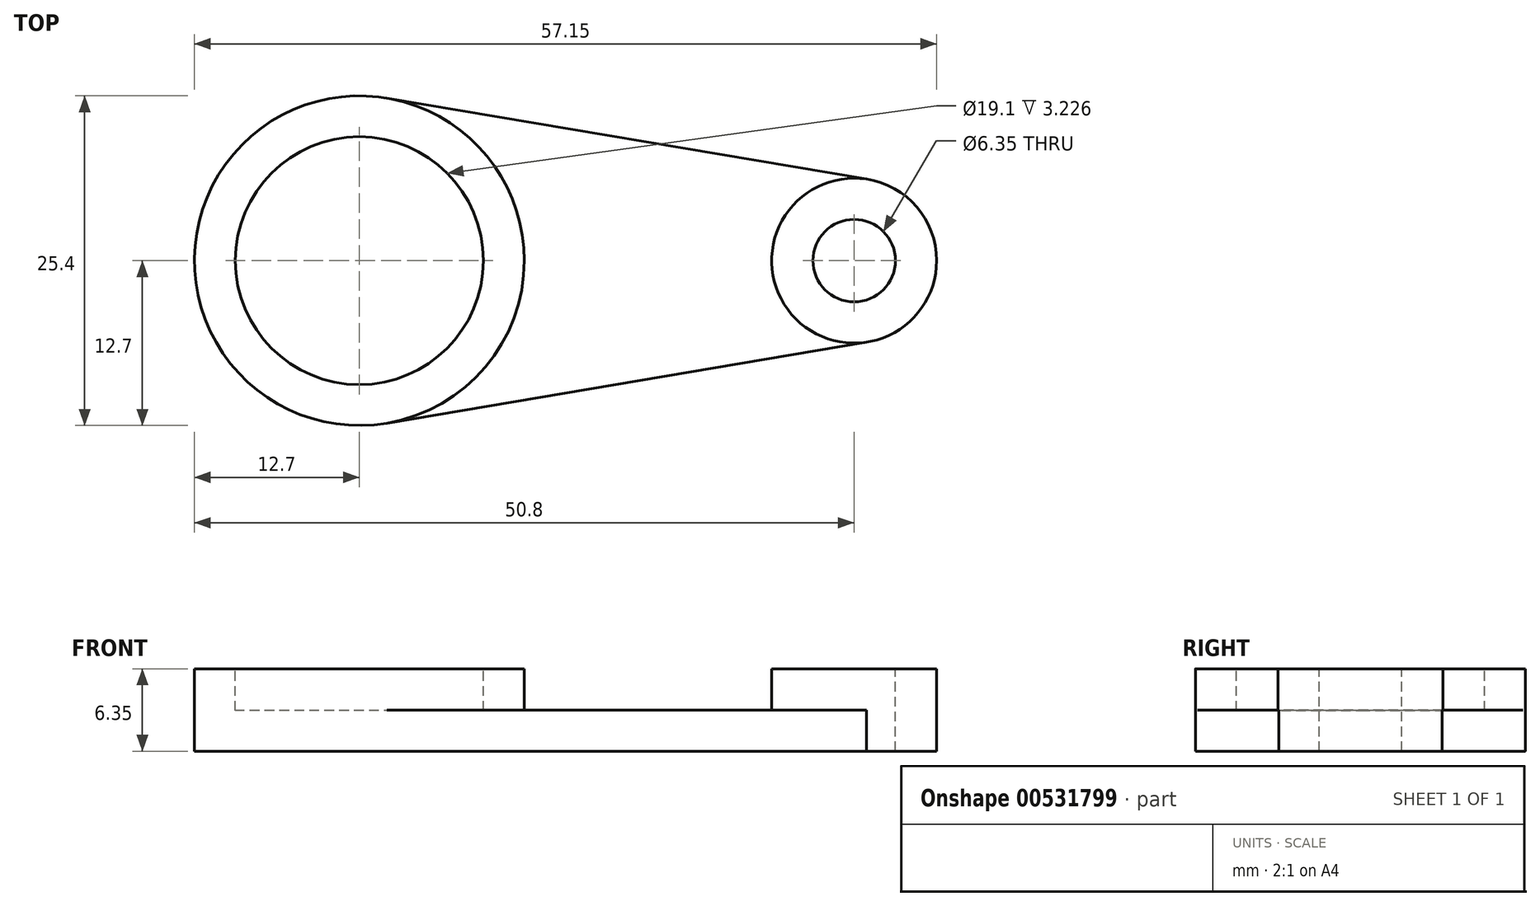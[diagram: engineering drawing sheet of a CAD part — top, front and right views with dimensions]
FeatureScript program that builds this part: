
annotation { "Feature Type Name" : "Feature", "Feature Type Description" : "" }
export const myFeature = defineFeature(function(context is Context, id is Id, definition is map)
    precondition{}
    {
        {
            var Q0;
            Q0=qCreatedBy(makeId("Top.planeOp"),FACE);
            var sketch = newSketch(context, id + "F0", { "sketchPlane" : qUnion([Q0])});
            skCircle(sketch, "E0", {"center": v(0, 0) * mm, "radius": 12.7 * mm});
            skCircle(sketch, "E1", {"center": v(38.1, 0) * mm, "radius": 6.35 * mm});
            skLineSegment(sketch, "E2", {"start": v(39.05, -6.28) * mm, "end": v(2.12, -12.52) * mm});
            skLineSegment(sketch, "E3", {"start": v(2.12, 12.52) * mm, "end": v(39.05, 6.28) * mm});
            skSolve(sketch);
        }
        {
            var Q0;
            Q0 = qSketchRegion(id + "F0", true);
            extrude(context, id + "F1", {"entities" : qUnion([Q0]), "depth" : 3.17 * mm, "offsetDistance" : 25.4 * mm});
        }
        {
            var Q0;
            Q0=makeQuery(id+"F1.opExtrude","CAP_FACE",FACE,{"disambiguationData":[OSD([sQuery(id+"F0.wireOp",EDGE,"E0"),sQuery(id+"F0.wireOp",EDGE,"E1"),sQuery(id+"F0.wireOp",EDGE,"E2"),sQuery(id+"F0.wireOp",EDGE,"E3")])],"isStart":false});
            var sketch = newSketch(context, id + "F2", { "sketchPlane" : qUnion([Q0])});
            skArc(sketch, "E4.0", {"start": v(39.05, -6.28) * mm, "mid": v(44.45, 0) * mm, "end": v(39.05, 6.28) * mm});
            skCircle(sketch, "E5", {"center": v(38.1, 0) * mm, "radius": 6.35 * mm});
            skArc(sketch, "E6.0", {"start": v(2.12, 12.52) * mm, "mid": v(-12.7, 0) * mm, "end": v(2.12, -12.52) * mm});
            skCircle(sketch, "E7", {"center": v(0, 0) * mm, "radius": 12.7 * mm});
            skSolve(sketch);
        }
        {
            var Q0;
            Q0 = qSketchRegion(id + "F2", true);
            extrude(context, id + "F3", {"entities" : qUnion([Q0]), "operationType" : NewBodyOperationType.ADD, "depth" : 3.17 * mm, "offsetDistance" : 25.4 * mm});
        }
        {
            var Q0;
            Q0=makeQuery(id+"F3.opExtrude","CAP_FACE",FACE,{"disambiguationData":[OSD([sQuery(id+"F2.wireOp",EDGE,"E7")])],"isStart":false});
            var sketch = newSketch(context, id + "F4", { "sketchPlane" : qUnion([Q0])});
            skCircle(sketch, "E8", {"center": v(0, 0) * mm, "radius": 9.55 * mm});
            skSolve(sketch);
        }
        {
            var Q0;
            Q0 = qSketchRegion(id + "F4", true);
            extrude(context, id + "F5", {"entities" : qUnion([Q0]), "operationType" : NewBodyOperationType.REMOVE, "oppositeDirection" : true, "depth" : 3.23 * mm, "offsetDistance" : 25.4 * mm});
        }
        {
            var Q0;
            Q0=makeQuery(id+"F3.opExtrude","CAP_FACE",FACE,{"disambiguationData":[OSD([sQuery(id+"F2.wireOp",EDGE,"E5")])],"isStart":false});
            var sketch = newSketch(context, id + "F6", { "sketchPlane" : qUnion([Q0])});
            skCircle(sketch, "E9", {"center": v(38.1, 0) * mm, "radius": 3.18 * mm});
            skSolve(sketch);
        }
        {
            var Q0;
            Q0=makeQuery(id+"F6.imprint","IMPRINT",FACE,{"disambiguationData":[TD([[makeQuery(id+"F6.imprint","IMPRINT",EDGE,{"derivedFrom":sQuery(id+"F6.wireOp",EDGE,"E9")}),1.0]])]});
            extrude(context, id + "F7", {"entities" : qUnion([Q0]), "operationType" : NewBodyOperationType.REMOVE, "endBound" : BoundingType.THROUGH_ALL, "oppositeDirection" : true, "depth" : 25.4 * mm, "offsetDistance" : 25.4 * mm});
        }
    });
